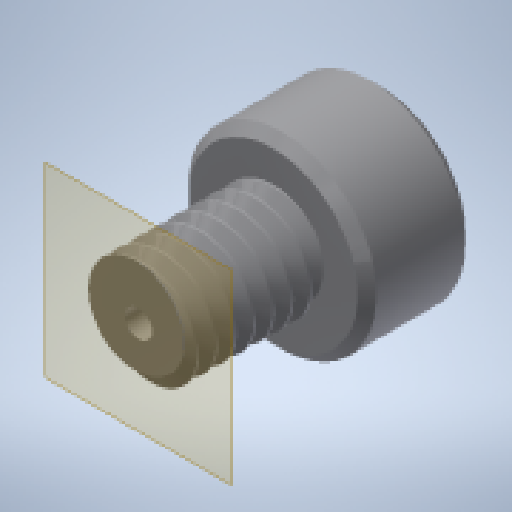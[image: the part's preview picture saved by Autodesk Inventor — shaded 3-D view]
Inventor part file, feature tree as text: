
AUTODESK INVENTOR PART (.ipt)
format: ipt  version: 2023 (Build 270158000, 158)  size: 596,992 bytes
history: native  units: in
note: dims shown in document units (in); Inventor stores cm internally (conversion verified against a paired STEP export)
features: split x2, plane x1, other x1
ambient origin geometry x8: Origin, YZ Plane, XZ Plane, XY Plane, X Axis, Y Axis, Z Axis, Center Point
bodies: Solid1 (feature_tree)
feature tree (4):
  plane  "Work Plane1"
  split  "Split1"
  split  "Split2"
  other  "Cut-Extrude3"
